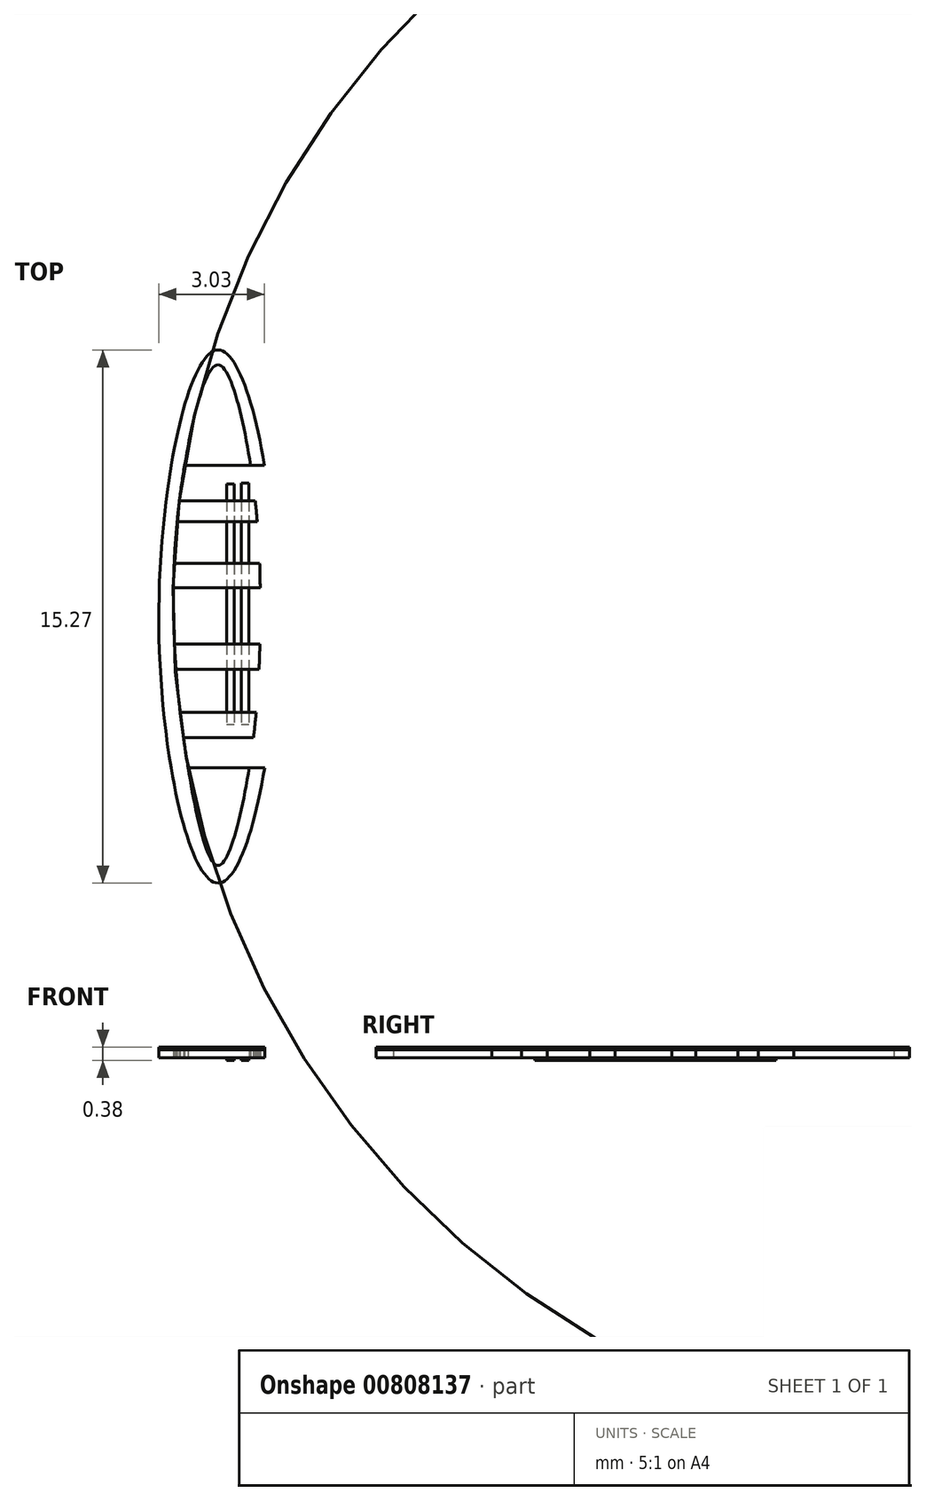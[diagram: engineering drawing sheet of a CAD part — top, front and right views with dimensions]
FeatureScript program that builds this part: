
annotation { "Feature Type Name" : "Feature", "Feature Type Description" : "" }
export const myFeature = defineFeature(function(context is Context, id is Id, definition is map)
    precondition{}
    {
        {
            var Q0;
            Q0=qCreatedBy(makeId("Top.planeOp"),FACE);
            var sketch = newSketch(context, id + "F0", { "sketchPlane" : qUnion([Q0])});
            skFitSpline(sketch, "E0", {"points": [v(0, 7.67) * mm, v(1.68, 0) * mm, v(0, -7.6) * mm, v(-1.7, 0) * mm, v(0, 7.67) * mm]});
            skLineSegment(sketch, "E1", {"start": v(0, 7.67) * mm, "end": v(0, 4.36) * mm});
            skLineSegment(sketch, "E2", {"start": v(0, -7.6) * mm, "end": v(0, -4.3) * mm});
            skLineSegment(sketch, "E3", {"start": v(0, -4.3) * mm, "end": v(1.33, -4.3) * mm});
            skLineSegment(sketch, "E4", {"start": v(1.33, -4.3) * mm, "end": v(-1.35, -4.3) * mm});
            skLineSegment(sketch, "E5", {"start": v(0, 4.36) * mm, "end": v(1.33, 4.36) * mm});
            skLineSegment(sketch, "E6", {"start": v(1.33, 4.36) * mm, "end": v(-1.34, 4.36) * mm});
            skFitSpline(sketch, "E7", {"points": [v(0, 7.24) * mm, v(-0.96, 4.36) * mm, v(-1.27, 0) * mm, v(-0.86, -4.3) * mm, v(0, -7.1) * mm, v(0.9, -4.3) * mm, v(1.2, 0) * mm, v(0.93, 4.36) * mm, v(0, 7.24) * mm]});
            skLineSegment(sketch, "E8", {"start": v(-1.1, 3.35) * mm, "end": v(1.07, 3.35) * mm});
            skLineSegment(sketch, "E9", {"start": v(-1.17, 2.75) * mm, "end": v(1.12, 2.75) * mm});
            skLineSegment(sketch, "E10", {"start": v(-1.26, 1.55) * mm, "end": v(1.2, 1.55) * mm});
            skLineSegment(sketch, "E11", {"start": v(-1.28, 0.86) * mm, "end": v(1.2, 0.86) * mm});
            skLineSegment(sketch, "E12", {"start": v(-1.25, -0.75) * mm, "end": v(1.2, -0.75) * mm});
            skLineSegment(sketch, "E13", {"start": v(-1.2, -1.48) * mm, "end": v(1.17, -1.48) * mm});
            skLineSegment(sketch, "E14", {"start": v(-1.09, -2.7) * mm, "end": v(1.1, -2.7) * mm});
            skLineSegment(sketch, "E15", {"start": v(-1, -3.44) * mm, "end": v(1.01, -3.44) * mm});
            skSolve(sketch);
        }
        {
            var Q0;
            {var subQ0=sQuery(id+"F0.wireOp",EDGE,"E1");var subQ1=sQuery(id+"F0.wireOp",EDGE,"E0");var subQ2=makeQuery(id+"F0.imprint","INTERSECT",VERTEX,{"derivedFrom":[subQ1,subQ0]});Q0=makeQuery(id+"F0.imprint","IMPRINT",FACE,{"disambiguationData":[TD([[makeQuery(id+"F0.imprint","IMPRINT",EDGE,{"disambiguationData":[TD([[subQ2,1.0]])],"derivedFrom":subQ1}),-1.0]])]});}
            var Q1;
            {var subQ0=sQuery(id+"F0.wireOp",EDGE,"E6");var subQ1=sQuery(id+"F0.wireOp",EDGE,"E1");var subQ2=makeQuery(id+"F0.imprint","INTERSECT",VERTEX,{"derivedFrom":[subQ1,subQ0]});Q1=makeQuery(id+"F0.imprint","IMPRINT",FACE,{"disambiguationData":[TD([[makeQuery(id+"F0.imprint","IMPRINT",EDGE,{"disambiguationData":[TD([[subQ2,1.0]])],"derivedFrom":subQ1}),-1.0]])]});}
            var Q2;
            {var subQ0=sQuery(id+"F0.wireOp",EDGE,"E6");var subQ1=sQuery(id+"F0.wireOp",EDGE,"E1");var subQ2=makeQuery(id+"F0.imprint","INTERSECT",VERTEX,{"derivedFrom":[subQ1,subQ0]});Q2=makeQuery(id+"F0.imprint","IMPRINT",FACE,{"disambiguationData":[TD([[makeQuery(id+"F0.imprint","IMPRINT",EDGE,{"disambiguationData":[TD([[subQ2,1.0]])],"derivedFrom":subQ1}),1.0]])]});}
            var Q3;
            {var subQ0=sQuery(id+"F0.wireOp",EDGE,"E1");var subQ1=sQuery(id+"F0.wireOp",EDGE,"E0");var subQ2=makeQuery(id+"F0.imprint","INTERSECT",VERTEX,{"derivedFrom":[subQ1,subQ0]});Q3=makeQuery(id+"F0.imprint","IMPRINT",FACE,{"disambiguationData":[TD([[makeQuery(id+"F0.imprint","IMPRINT",EDGE,{"disambiguationData":[TD([[subQ2,-1.0]])],"derivedFrom":subQ1}),-1.0]])]});}
            var Q4;
            {var subQ5=sQuery(id+"F0.wireOp",EDGE,"E4");var subQ6=sQuery(id+"F0.wireOp",EDGE,"E0");var subQ7=makeQuery(id+"F0.imprint","INTERSECT",VERTEX,{"disambiguationData":[OD(0.0)],"derivedFrom":[subQ6,subQ5]});Q4=makeQuery(id+"F0.imprint","IMPRINT",FACE,{"disambiguationData":[TD([[makeQuery(id+"F0.imprint","IMPRINT",EDGE,{"disambiguationData":[TD([[subQ7,1.0]])],"derivedFrom":subQ6}),-1.0]])]});}
            var Q5;
            {var subQ0=sQuery(id+"F0.wireOp",EDGE,"E8");Q5=makeQuery(id+"F0.imprint","IMPRINT",FACE,{"disambiguationData":[TD([[makeQuery(id+"F0.imprint","IMPRINT",EDGE,{"derivedFrom":subQ0}),-1.0]])]});}
            var Q6;
            {var subQ8=sQuery(id+"F0.wireOp",EDGE,"E4");var subQ9=sQuery(id+"F0.wireOp",EDGE,"E0");var subQ10=makeQuery(id+"F0.imprint","INTERSECT",VERTEX,{"disambiguationData":[OD(1.0)],"derivedFrom":[subQ9,subQ8]});Q6=makeQuery(id+"F0.imprint","IMPRINT",FACE,{"disambiguationData":[TD([[makeQuery(id+"F0.imprint","IMPRINT",EDGE,{"disambiguationData":[TD([[subQ10,-1.0]])],"derivedFrom":subQ9}),-1.0]])]});}
            var Q7;
            {var subQ0=sQuery(id+"F0.wireOp",EDGE,"E10");Q7=makeQuery(id+"F0.imprint","IMPRINT",FACE,{"disambiguationData":[TD([[makeQuery(id+"F0.imprint","IMPRINT",EDGE,{"derivedFrom":subQ0}),-1.0]])]});}
            var Q8;
            {var subQ0=sQuery(id+"F0.wireOp",EDGE,"E12");Q8=makeQuery(id+"F0.imprint","IMPRINT",FACE,{"disambiguationData":[TD([[makeQuery(id+"F0.imprint","IMPRINT",EDGE,{"derivedFrom":subQ0}),-1.0]])]});}
            var Q9;
            {var subQ0=sQuery(id+"F0.wireOp",EDGE,"E14");Q9=makeQuery(id+"F0.imprint","IMPRINT",FACE,{"disambiguationData":[TD([[makeQuery(id+"F0.imprint","IMPRINT",EDGE,{"derivedFrom":subQ0}),-1.0]])]});}
            var Q10;
            {var subQ0=sQuery(id+"F0.wireOp",EDGE,"E4");var subQ1=sQuery(id+"F0.wireOp",EDGE,"E2");var subQ2=makeQuery(id+"F0.imprint","INTERSECT",VERTEX,{"derivedFrom":[subQ1,subQ0]});Q10=makeQuery(id+"F0.imprint","IMPRINT",FACE,{"disambiguationData":[TD([[makeQuery(id+"F0.imprint","IMPRINT",EDGE,{"disambiguationData":[TD([[subQ2,1.0]])],"derivedFrom":subQ1}),1.0]])]});}
            var Q11;
            {var subQ0=sQuery(id+"F0.wireOp",EDGE,"E4");var subQ1=sQuery(id+"F0.wireOp",EDGE,"E2");var subQ2=makeQuery(id+"F0.imprint","INTERSECT",VERTEX,{"derivedFrom":[subQ1,subQ0]});Q11=makeQuery(id+"F0.imprint","IMPRINT",FACE,{"disambiguationData":[TD([[makeQuery(id+"F0.imprint","IMPRINT",EDGE,{"disambiguationData":[TD([[subQ2,1.0]])],"derivedFrom":subQ1}),-1.0]])]});}
            var Q12;
            {var subQ0=sQuery(id+"F0.wireOp",EDGE,"E2");var subQ1=sQuery(id+"F0.wireOp",EDGE,"E0");var subQ2=makeQuery(id+"F0.imprint","INTERSECT",VERTEX,{"derivedFrom":[subQ1,subQ0]});Q12=makeQuery(id+"F0.imprint","IMPRINT",FACE,{"disambiguationData":[TD([[makeQuery(id+"F0.imprint","IMPRINT",EDGE,{"disambiguationData":[TD([[subQ2,1.0]])],"derivedFrom":subQ1}),-1.0]])]});}
            var Q13;
            {var subQ0=sQuery(id+"F0.wireOp",EDGE,"E2");var subQ1=sQuery(id+"F0.wireOp",EDGE,"E0");var subQ2=makeQuery(id+"F0.imprint","INTERSECT",VERTEX,{"derivedFrom":[subQ1,subQ0]});Q13=makeQuery(id+"F0.imprint","IMPRINT",FACE,{"disambiguationData":[TD([[makeQuery(id+"F0.imprint","IMPRINT",EDGE,{"disambiguationData":[TD([[subQ2,-1.0]])],"derivedFrom":subQ1}),-1.0]])]});}
            extrude(context, id + "F1", {"entities" : qUnion([Q0, Q1, Q2, Q3, Q4, Q5, Q6, Q7, Q8, Q9, Q10, Q11, Q12, Q13]), "depth" : 0.23 * mm, "offsetDistance" : 25.4 * mm});
        }
        {
            var Q0;
            {var subQ8=sQuery(id+"F0.wireOp",EDGE,"E4");var subQ9=sQuery(id+"F0.wireOp",EDGE,"E0");var subQ10=makeQuery(id+"F0.imprint","INTERSECT",VERTEX,{"disambiguationData":[OD(1.0)],"derivedFrom":[subQ9,subQ8]});Q0=makeQuery(id+"F0.imprint","IMPRINT",FACE,{"disambiguationData":[TD([[makeQuery(id+"F0.imprint","IMPRINT",EDGE,{"disambiguationData":[TD([[subQ10,-1.0]])],"derivedFrom":subQ9}),-1.0]])]});}
            var Q1;
            {var subQ5=sQuery(id+"F0.wireOp",EDGE,"E4");var subQ6=sQuery(id+"F0.wireOp",EDGE,"E0");var subQ7=makeQuery(id+"F0.imprint","INTERSECT",VERTEX,{"disambiguationData":[OD(0.0)],"derivedFrom":[subQ6,subQ5]});Q1=makeQuery(id+"F0.imprint","IMPRINT",FACE,{"disambiguationData":[TD([[makeQuery(id+"F0.imprint","IMPRINT",EDGE,{"disambiguationData":[TD([[subQ7,1.0]])],"derivedFrom":subQ6}),-1.0]])]});}
            var Q2;
            {var subQ0=sQuery(id+"F0.wireOp",EDGE,"E1");var subQ1=sQuery(id+"F0.wireOp",EDGE,"E0");var subQ2=makeQuery(id+"F0.imprint","INTERSECT",VERTEX,{"derivedFrom":[subQ1,subQ0]});Q2=makeQuery(id+"F0.imprint","IMPRINT",FACE,{"disambiguationData":[TD([[makeQuery(id+"F0.imprint","IMPRINT",EDGE,{"disambiguationData":[TD([[subQ2,-1.0]])],"derivedFrom":subQ1}),-1.0]])]});}
            var Q3;
            {var subQ0=sQuery(id+"F0.wireOp",EDGE,"E1");var subQ1=sQuery(id+"F0.wireOp",EDGE,"E0");var subQ2=makeQuery(id+"F0.imprint","INTERSECT",VERTEX,{"derivedFrom":[subQ1,subQ0]});Q3=makeQuery(id+"F0.imprint","IMPRINT",FACE,{"disambiguationData":[TD([[makeQuery(id+"F0.imprint","IMPRINT",EDGE,{"disambiguationData":[TD([[subQ2,1.0]])],"derivedFrom":subQ1}),-1.0]])]});}
            var Q4;
            {var subQ0=sQuery(id+"F0.wireOp",EDGE,"E2");var subQ1=sQuery(id+"F0.wireOp",EDGE,"E0");var subQ2=makeQuery(id+"F0.imprint","INTERSECT",VERTEX,{"derivedFrom":[subQ1,subQ0]});Q4=makeQuery(id+"F0.imprint","IMPRINT",FACE,{"disambiguationData":[TD([[makeQuery(id+"F0.imprint","IMPRINT",EDGE,{"disambiguationData":[TD([[subQ2,-1.0]])],"derivedFrom":subQ1}),-1.0]])]});}
            var Q5;
            {var subQ0=sQuery(id+"F0.wireOp",EDGE,"E2");var subQ1=sQuery(id+"F0.wireOp",EDGE,"E0");var subQ2=makeQuery(id+"F0.imprint","INTERSECT",VERTEX,{"derivedFrom":[subQ1,subQ0]});Q5=makeQuery(id+"F0.imprint","IMPRINT",FACE,{"disambiguationData":[TD([[makeQuery(id+"F0.imprint","IMPRINT",EDGE,{"disambiguationData":[TD([[subQ2,1.0]])],"derivedFrom":subQ1}),-1.0]])]});}
            extrude(context, id + "F2", {"entities" : qUnion([Q0, Q1, Q2, Q3, Q4, Q5]), "depth" : 0.3 * mm, "offsetDistance" : 25.4 * mm});
        }
        {
            var Q0;
            Q0=qCreatedBy(makeId("Top.planeOp"),FACE);
            var sketch = newSketch(context, id + "F3", { "sketchPlane" : qUnion([Q0])});
            skLineSegment(sketch, "E16.bottom", {"start": v(0.25, 3.84) * mm, "end": v(0.47, 3.84) * mm});
            skLineSegment(sketch, "E16.top", {"start": v(0.25, -3.05) * mm, "end": v(0.47, -3.05) * mm});
            skLineSegment(sketch, "E16.left", {"start": v(0.25, 3.84) * mm, "end": v(0.25, -3.05) * mm});
            skLineSegment(sketch, "E16.right", {"start": v(0.47, 3.84) * mm, "end": v(0.47, -3.05) * mm});
            skLineSegment(sketch, "E17.bottom", {"start": v(0.66, 3.85) * mm, "end": v(0.88, 3.85) * mm});
            skLineSegment(sketch, "E17.top", {"start": v(0.66, -3.05) * mm, "end": v(0.88, -3.05) * mm});
            skLineSegment(sketch, "E17.left", {"start": v(0.66, 3.85) * mm, "end": v(0.66, -3.05) * mm});
            skLineSegment(sketch, "E17.right", {"start": v(0.88, 3.85) * mm, "end": v(0.88, -3.05) * mm});
            skSolve(sketch);
        }
        {
            var Q0;
            Q0=makeQuery(id+"F3.imprint","IMPRINT",FACE,{"disambiguationData":[TD([[makeQuery(id+"F3.imprint","IMPRINT",EDGE,{"derivedFrom":sQuery(id+"F3.wireOp",EDGE,"E16.bottom")}),-1.0]])]});
            var Q1;
            Q1=makeQuery(id+"F3.imprint","IMPRINT",FACE,{"disambiguationData":[TD([[makeQuery(id+"F3.imprint","IMPRINT",EDGE,{"derivedFrom":sQuery(id+"F3.wireOp",EDGE,"E17.bottom")}),-1.0]])]});
            extrude(context, id + "F4", {"entities" : qUnion([Q0, Q1]), "operationType" : NewBodyOperationType.ADD, "oppositeDirection" : true, "depth" : 0.08 * mm, "offsetDistance" : 25.4 * mm});
        }
    });
